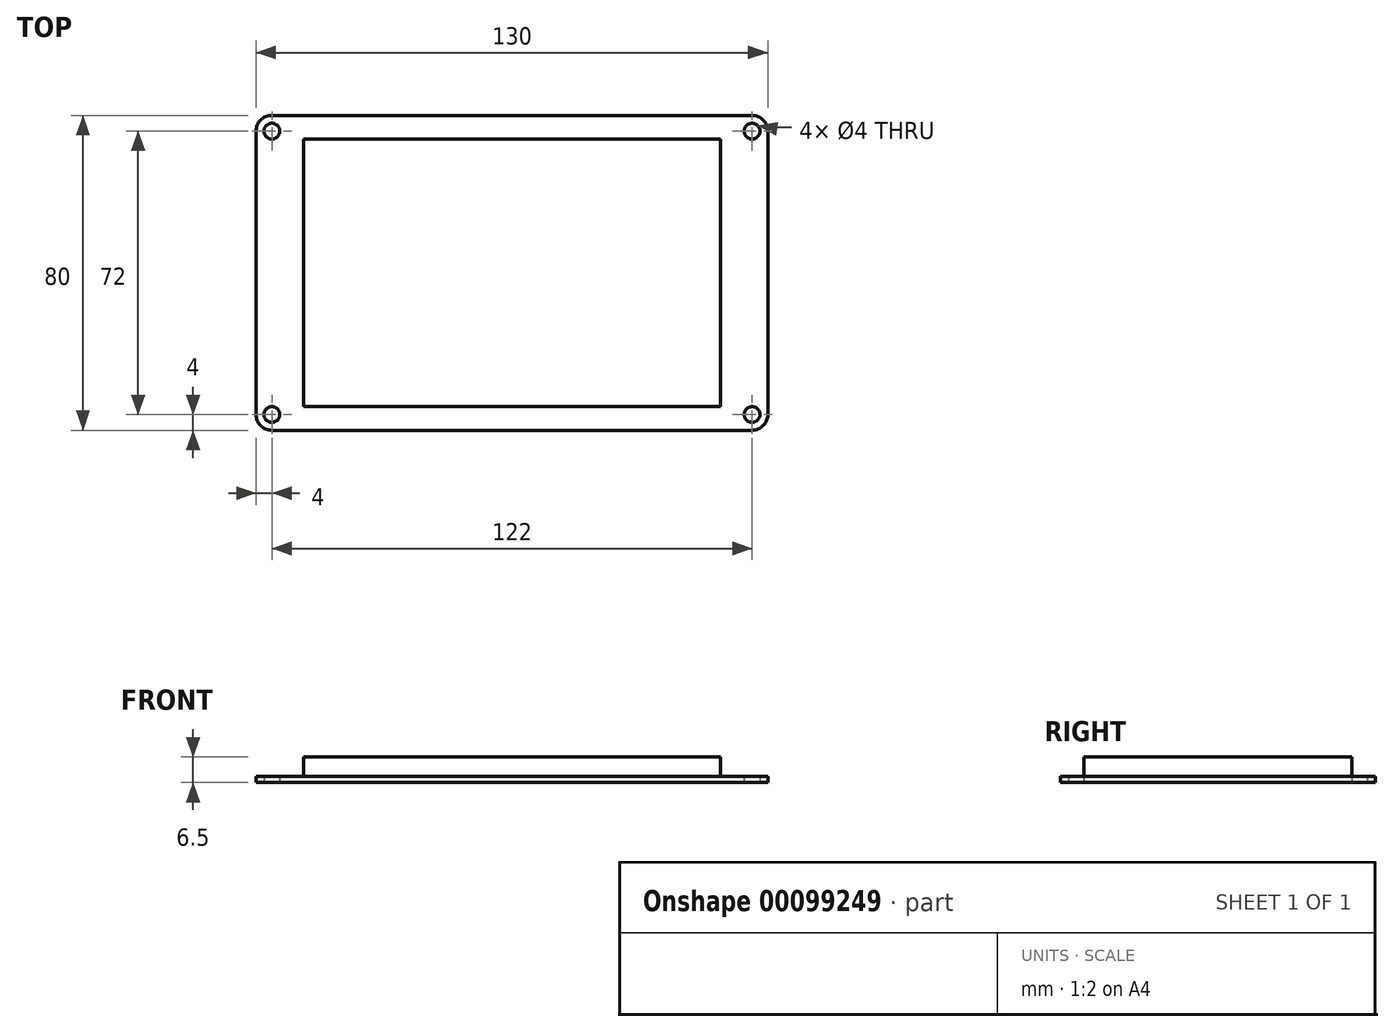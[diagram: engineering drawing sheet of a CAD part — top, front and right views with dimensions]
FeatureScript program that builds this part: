
annotation { "Feature Type Name" : "Feature", "Feature Type Description" : "" }
export const myFeature = defineFeature(function(context is Context, id is Id, definition is map)
    precondition{}
    {
        {
            var Q0;
            Q0=qCreatedBy(makeId("Top.planeOp"),FACE);
            var sketch = newSketch(context, id + "F0", { "sketchPlane" : qUnion([Q0])});
            skLineSegment(sketch, "E0.bottom", {"start": v(4, 0) * mm, "end": v(126, 0) * mm});
            skLineSegment(sketch, "E0.top", {"start": v(4, 80) * mm, "end": v(126, 80) * mm});
            skLineSegment(sketch, "E0.left", {"start": v(0, 4) * mm, "end": v(0, 76) * mm});
            skLineSegment(sketch, "E0.right", {"start": v(130, 4) * mm, "end": v(130, 76) * mm});
            skPoint(sketch, "E1.visualSharp", {"position": v(0, 0) * mm});
            skArc(sketch, "E1.filletArc", {"start": v(0, 4) * mm, "mid": v(1.17, 1.17) * mm, "end": v(4, 0) * mm});
            skPoint(sketch, "E2.visualSharp", {"position": v(0, 80) * mm});
            skArc(sketch, "E2.filletArc", {"start": v(4, 80) * mm, "mid": v(1.17, 78.83) * mm, "end": v(0, 76) * mm});
            skPoint(sketch, "E3.visualSharp", {"position": v(130, 80) * mm});
            skArc(sketch, "E3.filletArc", {"start": v(130, 76) * mm, "mid": v(128.83, 78.83) * mm, "end": v(126, 80) * mm});
            skPoint(sketch, "E4.visualSharp", {"position": v(130, 0) * mm});
            skArc(sketch, "E4.filletArc", {"start": v(126, 0) * mm, "mid": v(128.83, 1.17) * mm, "end": v(130, 4) * mm});
            skCircle(sketch, "E5", {"center": v(4, 4) * mm, "radius": 2 * mm});
            skCircle(sketch, "E6.MirrorC", {"center": v(4, 76) * mm, "radius": 2 * mm});
            skCircle(sketch, "E7.MirrorC", {"center": v(126, 76) * mm, "radius": 2 * mm});
            skCircle(sketch, "E8.MirrorC", {"center": v(126, 4) * mm, "radius": 2 * mm});
            skSolve(sketch);
        }
        {
            var Q0;
            Q0 = qSketchRegion(id + "F0", true);
            extrude(context, id + "F1", {"entities" : qUnion([Q0]), "depth" : 1.5 * mm});
        }
        {
            var Q0;
            Q0=makeQuery(id+"F1.opExtrude","CAP_FACE",FACE,{"disambiguationData":[OSD([sQuery(id+"F0.wireOp",EDGE,"E0.bottom"),sQuery(id+"F0.wireOp",EDGE,"E0.top"),sQuery(id+"F0.wireOp",EDGE,"E0.left"),sQuery(id+"F0.wireOp",EDGE,"E0.right"),sQuery(id+"F0.wireOp",EDGE,"E1.filletArc"),sQuery(id+"F0.wireOp",EDGE,"E2.filletArc"),sQuery(id+"F0.wireOp",EDGE,"E3.filletArc"),sQuery(id+"F0.wireOp",EDGE,"E4.filletArc"),sQuery(id+"F0.wireOp",EDGE,"E5"),sQuery(id+"F0.wireOp",EDGE,"E6.MirrorC"),sQuery(id+"F0.wireOp",EDGE,"E7.MirrorC"),sQuery(id+"F0.wireOp",EDGE,"E8.MirrorC")])],"isStart":false});
            var sketch = newSketch(context, id + "F2", { "sketchPlane" : qUnion([Q0])});
            skLineSegment(sketch, "E9.bottom", {"start": v(12, 6) * mm, "end": v(118, 6) * mm});
            skLineSegment(sketch, "E9.top", {"start": v(12, 74) * mm, "end": v(118, 74) * mm});
            skLineSegment(sketch, "E9.left", {"start": v(12, 6) * mm, "end": v(12, 74) * mm});
            skLineSegment(sketch, "E9.right", {"start": v(118, 6) * mm, "end": v(118, 74) * mm});
            skSolve(sketch);
        }
        {
            var Q0;
            Q0 = qSketchRegion(id + "F2", true);
            extrude(context, id + "F3", {"entities" : qUnion([Q0]), "depth" : 5 * mm});
        }
    });
